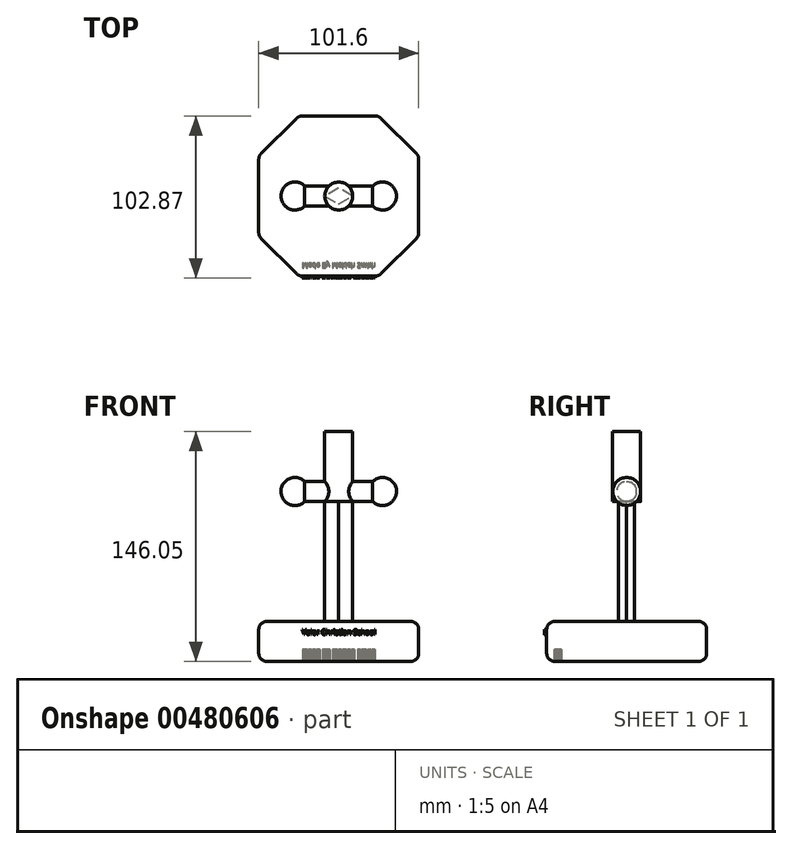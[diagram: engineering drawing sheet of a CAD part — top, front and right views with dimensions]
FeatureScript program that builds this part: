
annotation { "Feature Type Name" : "Feature", "Feature Type Description" : "" }
export const myFeature = defineFeature(function(context is Context, id is Id, definition is map)
    precondition{}
    {
        {
            var Q0;
            Q0=qCreatedBy(makeId("Front.planeOp"),FACE);
            var sketch = newSketch(context, id + "F0", { "sketchPlane" : qUnion([Q0])});
            skLineSegment(sketch, "E0", {"start": v(-8.9, 0) * mm, "end": v(-8.9, 76.2) * mm});
            skLineSegment(sketch, "E1", {"start": v(8.89, 0) * mm, "end": v(8.89, 76.2) * mm});
            skLineSegment(sketch, "E2", {"start": v(-8.9, 76.2) * mm, "end": v(8.89, 76.2) * mm});
            skLineSegment(sketch, "E3", {"start": v(-8.9, 76.2) * mm, "end": v(-21.6, 76.2) * mm});
            skLineSegment(sketch, "E4", {"start": v(8.89, 76.2) * mm, "end": v(21.59, 76.2) * mm});
            skLineSegment(sketch, "E5", {"start": v(-21.6, 76.2) * mm, "end": v(-21.6, 88.9) * mm});
            skLineSegment(sketch, "E6", {"start": v(21.59, 76.2) * mm, "end": v(21.59, 88.9) * mm});
            skArc(sketch, "E7", {"start": v(-21.6, 88.9) * mm, "mid": v(-36.7, 82.55) * mm, "end": v(-21.6, 76.2) * mm});
            skArc(sketch, "E8", {"start": v(21.59, 76.2) * mm, "mid": v(36.7, 82.55) * mm, "end": v(21.59, 88.9) * mm});
            skLineSegment(sketch, "E9", {"start": v(-21.6, 88.9) * mm, "end": v(21.59, 88.9) * mm});
            skPoint(sketch, "E10", {"position": v(-8.9, 88.9) * mm});
            skPoint(sketch, "E11", {"position": v(8.89, 88.9) * mm});
            skLineSegment(sketch, "E12", {"start": v(-8.9, 88.9) * mm, "end": v(-8.9, 120.65) * mm});
            skLineSegment(sketch, "E13", {"start": v(8.89, 88.9) * mm, "end": v(8.89, 120.65) * mm});
            skArc(sketch, "E14", {"start": v(0, 139.26) * mm, "mid": v(-10.31, 132.76) * mm, "end": v(-8.9, 120.65) * mm});
            skLineSegment(sketch, "E15", {"start": v(-8.9, 120.65) * mm, "end": v(8.89, 120.65) * mm});
            skLineSegment(sketch, "E16", {"start": v(0, 139.26) * mm, "end": v(0, 88.9) * mm});
            skLineSegment(sketch, "E17", {"start": v(-36.7, 82.55) * mm, "end": v(36.7, 82.55) * mm});
            skArc(sketch, "E18.MirrorCS", {"start": v(0, 139.26) * mm, "mid": v(10.31, 132.76) * mm, "end": v(8.89, 120.65) * mm});
            skLineSegment(sketch, "E19", {"start": v(-8.9, 0) * mm, "end": v(8.89, 0) * mm});
            skLineSegment(sketch, "E20", {"start": v(8.89, 82.55) * mm, "end": v(8.89, 76.2) * mm});
            skLineSegment(sketch, "E21", {"start": v(-8.9, 82.55) * mm, "end": v(-8.9, 76.2) * mm});
            skLineSegment(sketch, "E22.trimOffspring", {"start": v(0, 82.55) * mm, "end": v(0, 0) * mm});
            skLineSegment(sketch, "E23", {"start": v(8.89, 82.55) * mm, "end": v(8.89, 88.9) * mm});
            skLineSegment(sketch, "E24", {"start": v(-8.9, 82.55) * mm, "end": v(-8.9, 88.9) * mm});
            skLineSegment(sketch, "E25", {"start": v(0, 82.55) * mm, "end": v(0, 88.9) * mm});
            skSolve(sketch);
        }
        {
            var Q0;
            {var subQ0=sQuery(id+"F0.wireOp",EDGE,"E18.MirrorCS");Q0=makeQuery(id+"F0.imprint","IMPRINT",FACE,{"disambiguationData":[TD([[makeQuery(id+"F0.imprint","IMPRINT",EDGE,{"derivedFrom":subQ0}),-1.0]])]});}
            var Q1;
            {var subQ0=sQuery(id+"F0.wireOp",EDGE,"E13");Q1=makeQuery(id+"F0.imprint","IMPRINT",FACE,{"disambiguationData":[TD([[makeQuery(id+"F0.imprint","IMPRINT",EDGE,{"derivedFrom":subQ0}),1.0]])]});}
            var Q2;
            {var subQ0=sQuery(id+"F0.wireOp",EDGE,"E20");Q2=makeQuery(id+"F0.imprint","IMPRINT",FACE,{"disambiguationData":[TD([[makeQuery(id+"F0.imprint","IMPRINT",EDGE,{"derivedFrom":subQ0}),-1.0]])]});}
            var Q3;
            {var subQ0=sQuery(id+"F0.wireOp",EDGE,"E23");Q3=makeQuery(id+"F0.imprint","IMPRINT",FACE,{"disambiguationData":[TD([[makeQuery(id+"F0.imprint","IMPRINT",EDGE,{"derivedFrom":subQ0}),1.0]])]});}
            var Q4;
            Q4=sQuery(id+"F0.wireOp",EDGE,"E16");
            revolve(context, id + "F1", {"entities" : qUnion([Q0, Q1, Q2, Q3]), "axis" : qUnion([Q4]), "revolveType" : RevolveType.FULL});
        }
        {
            var Q0;
            {var subQ0=sQuery(id+"F0.wireOp",EDGE,"E7");var subQ3=sQuery(id+"F0.wireOp",EDGE,"E17");var subQ5=makeQuery(id+"F0.imprint","INTERSECT",VERTEX,{"derivedFrom":[subQ0,subQ3]});Q0=makeQuery(id+"F0.imprint","IMPRINT",FACE,{"disambiguationData":[TD([[makeQuery(id+"F0.imprint","IMPRINT",EDGE,{"disambiguationData":[TD([[subQ5,-1.0]])],"derivedFrom":subQ3}),1.0]])]});}
            var Q1;
            {var subQ0=sQuery(id+"F0.wireOp",EDGE,"E8");var subQ3=sQuery(id+"F0.wireOp",EDGE,"E17");var subQ5=makeQuery(id+"F0.imprint","INTERSECT",VERTEX,{"derivedFrom":[subQ0,subQ3]});Q1=makeQuery(id+"F0.imprint","IMPRINT",FACE,{"disambiguationData":[TD([[makeQuery(id+"F0.imprint","IMPRINT",EDGE,{"disambiguationData":[TD([[subQ5,1.0]])],"derivedFrom":subQ3}),1.0]])]});}
            var Q2;
            {var subQ1=sQuery(id+"F0.wireOp",EDGE,"E6");var subQ3=sQuery(id+"F0.wireOp",EDGE,"E17");var subQ4=makeQuery(id+"F0.imprint","INTERSECT",VERTEX,{"derivedFrom":[subQ1,subQ3]});Q2=makeQuery(id+"F0.imprint","IMPRINT",FACE,{"disambiguationData":[TD([[makeQuery(id+"F0.imprint","IMPRINT",EDGE,{"disambiguationData":[TD([[subQ4,1.0]])],"derivedFrom":subQ3}),1.0]])]});}
            var Q3;
            {var subQ1=sQuery(id+"F0.wireOp",EDGE,"E5");var subQ3=sQuery(id+"F0.wireOp",EDGE,"E17");var subQ4=makeQuery(id+"F0.imprint","INTERSECT",VERTEX,{"derivedFrom":[subQ1,subQ3]});Q3=makeQuery(id+"F0.imprint","IMPRINT",FACE,{"disambiguationData":[TD([[makeQuery(id+"F0.imprint","IMPRINT",EDGE,{"disambiguationData":[TD([[subQ4,-1.0]])],"derivedFrom":subQ3}),1.0]])]});}
            var Q4;
            {var subQ0=sQuery(id+"F0.wireOp",EDGE,"E23");Q4=makeQuery(id+"F0.imprint","IMPRINT",FACE,{"disambiguationData":[TD([[makeQuery(id+"F0.imprint","IMPRINT",EDGE,{"derivedFrom":subQ0}),1.0]])]});}
            var Q5;
            {var subQ0=sQuery(id+"F0.wireOp",EDGE,"E24");Q5=makeQuery(id+"F0.imprint","IMPRINT",FACE,{"disambiguationData":[TD([[makeQuery(id+"F0.imprint","IMPRINT",EDGE,{"derivedFrom":subQ0}),-1.0]])]});}
            var Q6;
            Q6=sQuery(id+"F0.wireOp",EDGE,"E17");
            revolve(context, id + "F2", {"entities" : qUnion([Q0, Q1, Q2, Q3, Q4, Q5]), "axis" : qUnion([Q6]), "revolveType" : RevolveType.FULL});
        }
        {
            var Q0;
            {var subQ0=sQuery(id+"F0.wireOp",EDGE,"E1");Q0=makeQuery(id+"F0.imprint","IMPRINT",FACE,{"disambiguationData":[TD([[makeQuery(id+"F0.imprint","IMPRINT",EDGE,{"derivedFrom":subQ0}),1.0]])]});}
            var Q1;
            {var subQ0=sQuery(id+"F0.wireOp",EDGE,"E0");Q1=makeQuery(id+"F0.imprint","IMPRINT",FACE,{"disambiguationData":[TD([[makeQuery(id+"F0.imprint","IMPRINT",EDGE,{"derivedFrom":subQ0}),-1.0]])]});}
            extrude(context, id + "F3", {"entities" : qUnion([Q0, Q1]), "operationType" : NewBodyOperationType.ADD, "oppositeDirection" : true, "depth" : 7.62 * mm});
        }
        {
            var Q0;
            Q0=makeQuery(id+"F3.opExtrude","SWEPT_FACE",FACE,{"disambiguationData":[OSD([sQuery(id+"F0.wireOp",EDGE,"E19")])]});
            var sketch = newSketch(context, id + "F4", { "sketchPlane" : qUnion([Q0])});
            skPoint(sketch, "E26.end.orphan", {"position": v(0, -7.62) * mm});
            skLineSegment(sketch, "E27", {"start": v(0, 0) * mm, "end": v(8.89, 0) * mm});
            skLineSegment(sketch, "E28", {"start": v(8.89, 0) * mm, "end": v(0, -5.08) * mm});
            skLineSegment(sketch, "E29", {"start": v(0, -5.08) * mm, "end": v(-8.9, 0) * mm});
            skLineSegment(sketch, "E30", {"start": v(-8.9, 0) * mm, "end": v(0, 0) * mm});
            skLineSegment(sketch, "E31", {"start": v(0, 0) * mm, "end": v(0, -5.08) * mm});
            skSolve(sketch);
        }
        {
            var Q0;
            Q0=makeQuery(id+"F4.imprint","IMPRINT",FACE,{"disambiguationData":[TD([[makeQuery(id+"F4.imprint","IMPRINT",EDGE,{"derivedFrom":sQuery(id+"F4.wireOp",EDGE,"6hnVyOId-7ml1-uDIW-rOqS-Pi0ak5nLySGR")}),1.0]])]});
            var Q1;
            {var subQ0=sQuery(id+"F4.wireOp",EDGE,"mvX1mz3N-spie-N4J2-ecJO-cWR3p3tE930F");Q1=makeQuery(id+"F4.imprint","IMPRINT",FACE,{"disambiguationData":[TD([[makeQuery(id+"F4.imprint","IMPRINT",EDGE,{"derivedFrom":subQ0}),-1.0]])]});}
            var Q2;
            {var subQ0=sQuery(id+"F4.wireOp",EDGE,"dbcYeZqB-0URT-xalG-e7TK-n7e198GyKyVK");Q2=makeQuery(id+"F4.imprint","IMPRINT",FACE,{"disambiguationData":[TD([[makeQuery(id+"F4.imprint","IMPRINT",EDGE,{"derivedFrom":subQ0}),1.0]])]});}
            var Q3;
            Q3=makeQuery(id+"F4.imprint","IMPRINT",FACE,{"disambiguationData":[TD([[makeQuery(id+"F4.imprint","IMPRINT",EDGE,{"derivedFrom":sQuery(id+"F4.wireOp",EDGE,"E28")}),1.0]])]});
            extrude(context, id + "F5", {"entities" : qUnion([Q0, Q1, Q2, Q3]), "operationType" : NewBodyOperationType.REMOVE, "oppositeDirection" : true, "depth" : 76.2 * mm});
        }
        {
            var Q0;
            {var subQ0=sQuery(id+"F0.wireOp",EDGE,"E0");Q0=makeQuery(id+"F0.imprint","IMPRINT",FACE,{"disambiguationData":[TD([[makeQuery(id+"F0.imprint","IMPRINT",EDGE,{"derivedFrom":subQ0}),-1.0]])]});}
            var Q1;
            {var subQ0=sQuery(id+"F0.wireOp",EDGE,"E1");Q1=makeQuery(id+"F0.imprint","IMPRINT",FACE,{"disambiguationData":[TD([[makeQuery(id+"F0.imprint","IMPRINT",EDGE,{"derivedFrom":subQ0}),1.0]])]});}
            extrude(context, id + "F6", {"entities" : qUnion([Q0, Q1]), "operationType" : NewBodyOperationType.ADD, "depth" : 7.62 * mm});
        }
        {
            var Q0;
            {var subQ0=sQuery(id+"F0.wireOp",EDGE,"E19");Q0=makeQuery(id+"F6.boolean.opBoolean","MERGE",FACE,{"derivedFrom":[makeQuery(id+"F3.opExtrude","SWEPT_FACE",FACE,{"disambiguationData":[OSD([subQ0])]}),makeQuery(id+"F6.opExtrude","SWEPT_FACE",FACE,{"disambiguationData":[OSD([subQ0])]})]});}
            var sketch = newSketch(context, id + "F7", { "sketchPlane" : qUnion([Q0])});
            skLineSegment(sketch, "E32", {"start": v(0, 0) * mm, "end": v(0, 5.08) * mm});
            skLineSegment(sketch, "E33", {"start": v(-8.9, 0) * mm, "end": v(0, 5.08) * mm});
            skLineSegment(sketch, "E34", {"start": v(0, 5.08) * mm, "end": v(8.89, 0) * mm});
            skLineSegment(sketch, "E35", {"start": v(0, 0) * mm, "end": v(-8.9, 0) * mm});
            skLineSegment(sketch, "E36", {"start": v(0, 0) * mm, "end": v(8.89, 0) * mm});
            skSolve(sketch);
        }
        {
            var Q0;
            Q0=makeQuery(id+"F7.imprint","IMPRINT",FACE,{"disambiguationData":[TD([[makeQuery(id+"F7.imprint","IMPRINT",EDGE,{"derivedFrom":sQuery(id+"F7.wireOp",EDGE,"E33")}),1.0]])]});
            extrude(context, id + "F8", {"entities" : qUnion([Q0]), "operationType" : NewBodyOperationType.REMOVE, "oppositeDirection" : true, "depth" : 76.2 * mm});
        }
        {
            var Q0;
            Q0=qCreatedBy(makeId("Top.planeOp"),FACE);
            var sketch = newSketch(context, id + "F9", { "sketchPlane" : qUnion([Q0])});
            skLineSegment(sketch, "E37", {"start": v(0, 50.8) * mm, "end": v(0, 0) * mm});
            skLineSegment(sketch, "E38", {"start": v(0, 50.8) * mm, "end": v(-25.4, 50.8) * mm});
            skLineSegment(sketch, "E39.MirrorCS", {"start": v(0, 50.8) * mm, "end": v(25.4, 50.8) * mm});
            skLineSegment(sketch, "E40", {"start": v(0, 0) * mm, "end": v(50.8, 0) * mm});
            skLineSegment(sketch, "E41.MirrorCS", {"start": v(0, -50.8) * mm, "end": v(0, 0) * mm});
            skLineSegment(sketch, "E42.MirrorCS", {"start": v(0, 0) * mm, "end": v(-50.8, 0) * mm});
            skLineSegment(sketch, "E43.MirrorCS", {"start": v(0, -50.8) * mm, "end": v(-25.4, -50.8) * mm});
            skLineSegment(sketch, "E44.MirrorCS", {"start": v(0, -50.8) * mm, "end": v(25.4, -50.8) * mm});
            skLineSegment(sketch, "E45", {"start": v(-50.8, 0) * mm, "end": v(-50.8, 25.4) * mm});
            skLineSegment(sketch, "E46.MirrorCS", {"start": v(-50.8, 0) * mm, "end": v(-50.8, -25.4) * mm});
            skLineSegment(sketch, "E47.MirrorCS", {"start": v(50.8, 0) * mm, "end": v(50.8, 25.4) * mm});
            skLineSegment(sketch, "E48.MirrorCS", {"start": v(50.8, 0) * mm, "end": v(50.8, -25.4) * mm});
            skLineSegment(sketch, "E49", {"start": v(-50.8, 25.4) * mm, "end": v(-25.4, 50.8) * mm});
            skLineSegment(sketch, "E50", {"start": v(25.4, 50.8) * mm, "end": v(50.8, 25.4) * mm});
            skLineSegment(sketch, "E51", {"start": v(25.4, -50.8) * mm, "end": v(50.8, -25.4) * mm});
            skLineSegment(sketch, "E52", {"start": v(-25.4, -50.8) * mm, "end": v(-50.8, -25.4) * mm});
            skSolve(sketch);
        }
        {
            var Q0;
            Q0=makeQuery(id+"F9.imprint","IMPRINT",FACE,{"disambiguationData":[TD([[makeQuery(id+"F9.imprint","IMPRINT",EDGE,{"derivedFrom":sQuery(id+"F9.wireOp",EDGE,"E37")}),-1.0]])]});
            var Q1;
            Q1=makeQuery(id+"F9.imprint","IMPRINT",FACE,{"disambiguationData":[TD([[makeQuery(id+"F9.imprint","IMPRINT",EDGE,{"derivedFrom":sQuery(id+"F9.wireOp",EDGE,"E41.MirrorCS")}),1.0]])]});
            var Q2;
            Q2=makeQuery(id+"F9.imprint","IMPRINT",FACE,{"disambiguationData":[TD([[makeQuery(id+"F9.imprint","IMPRINT",EDGE,{"derivedFrom":sQuery(id+"F9.wireOp",EDGE,"E37")}),1.0]])]});
            var Q3;
            Q3=makeQuery(id+"F9.imprint","IMPRINT",FACE,{"disambiguationData":[TD([[makeQuery(id+"F9.imprint","IMPRINT",EDGE,{"derivedFrom":sQuery(id+"F9.wireOp",EDGE,"E40")}),-1.0]])]});
            extrude(context, id + "F10", {"entities" : qUnion([Q0, Q1, Q2, Q3]), "operationType" : NewBodyOperationType.ADD, "depth" : -25.4 * mm});
        }
        {
            var Q0;
            Q0=makeQuery(id+"F10.opExtrude","SWEPT_FACE",FACE,{"disambiguationData":[OSD([sQuery(id+"F9.wireOp",EDGE,"E52")])]});
            var Q1;
            Q1=makeQuery(id+"F10.opExtrude","SWEPT_FACE",FACE,{"disambiguationData":[OSD([sQuery(id+"F9.wireOp",EDGE,"E43.MirrorCS"),sQuery(id+"F9.wireOp",EDGE,"E44.MirrorCS")])]});
            var Q2;
            Q2=makeQuery(id+"F10.opExtrude","SWEPT_FACE",FACE,{"disambiguationData":[OSD([sQuery(id+"F9.wireOp",EDGE,"E49")])]});
            var Q3;
            Q3=makeQuery(id+"F10.opExtrude","SWEPT_FACE",FACE,{"disambiguationData":[OSD([sQuery(id+"F9.wireOp",EDGE,"E38"),sQuery(id+"F9.wireOp",EDGE,"E39.MirrorCS")])]});
            var Q4;
            Q4=makeQuery(id+"F10.opExtrude","SWEPT_FACE",FACE,{"disambiguationData":[OSD([sQuery(id+"F9.wireOp",EDGE,"E50")])]});
            var Q5;
            Q5=makeQuery(id+"F10.opExtrude","SWEPT_FACE",FACE,{"disambiguationData":[OSD([sQuery(id+"F9.wireOp",EDGE,"E47.MirrorCS"),sQuery(id+"F9.wireOp",EDGE,"E48.MirrorCS")])]});
            var Q6;
            Q6=makeQuery(id+"F10.opExtrude","SWEPT_FACE",FACE,{"disambiguationData":[OSD([sQuery(id+"F9.wireOp",EDGE,"E51")])]});
            var Q7;
            Q7=makeQuery(id+"F10.opExtrude","SWEPT_FACE",FACE,{"disambiguationData":[OSD([sQuery(id+"F9.wireOp",EDGE,"E45"),sQuery(id+"F9.wireOp",EDGE,"E46.MirrorCS")])]});
            fillet(context, id + "F11", {"entities" : qUnion([Q0, Q1, Q2, Q3, Q4, Q5, Q6, Q7]), "radius" : 5.08 * mm, "tangentPropagation" : true, "allowEdgeOverflow" : false});
        }
        {
            var Q0;
            Q0=makeQuery(id+"F10.opExtrude","SWEPT_FACE",FACE,{"disambiguationData":[OSD([sQuery(id+"F9.wireOp",EDGE,"E43.MirrorCS"),sQuery(id+"F9.wireOp",EDGE,"E44.MirrorCS")])]});
            var sketch = newSketch(context, id + "F12", { "sketchPlane" : qUnion([Q0])});
            skText(sketch, "E53", { "text": "Valor Christian School", "fontName": "OpenSans-Regular.ttf"});
            const initialGuessF12  = {"E53": [-0.0233, -0.00838, 1, 0, 0.0033]};
            skSetInitialGuess(sketch, initialGuessF12);
            skSolve(sketch);
        }
        {
            var Q0;
            Q0 = qSketchRegion(id + "F12", true);
            extrude(context, id + "F13", {"entities" : qUnion([Q0]), "operationType" : NewBodyOperationType.ADD, "depth" : 1.27 * mm});
        }
        {
            var Q0;
            Q0=makeQuery(id+"F10.opExtrude","CAP_FACE",FACE,{"disambiguationData":[OSD([sQuery(id+"F9.wireOp",EDGE,"E38"),sQuery(id+"F9.wireOp",EDGE,"E39.MirrorCS"),sQuery(id+"F9.wireOp",EDGE,"E43.MirrorCS"),sQuery(id+"F9.wireOp",EDGE,"E44.MirrorCS"),sQuery(id+"F9.wireOp",EDGE,"E45"),sQuery(id+"F9.wireOp",EDGE,"E46.MirrorCS"),sQuery(id+"F9.wireOp",EDGE,"E47.MirrorCS"),sQuery(id+"F9.wireOp",EDGE,"E48.MirrorCS"),sQuery(id+"F9.wireOp",EDGE,"E49"),sQuery(id+"F9.wireOp",EDGE,"E50"),sQuery(id+"F9.wireOp",EDGE,"E51"),sQuery(id+"F9.wireOp",EDGE,"E52")])],"isStart":false});
            var sketch = newSketch(context, id + "F14", { "sketchPlane" : qUnion([Q0])});
            skText(sketch, "E54", { "text": "Made By Mekiah Smith", "fontName": "OpenSans-Regular.ttf"});
            const initialGuessF14  = {"E54": [-0.0233, 0.04257, 1, 0, 0.00315]};
            skSetInitialGuess(sketch, initialGuessF14);
            skSolve(sketch);
        }
        {
            var Q0;
            Q0 = qSketchRegion(id + "F14", true);
            extrude(context, id + "F15", {"entities" : qUnion([Q0]), "operationType" : NewBodyOperationType.REMOVE, "oppositeDirection" : true, "depth" : 7.62 * mm});
        }
    });
